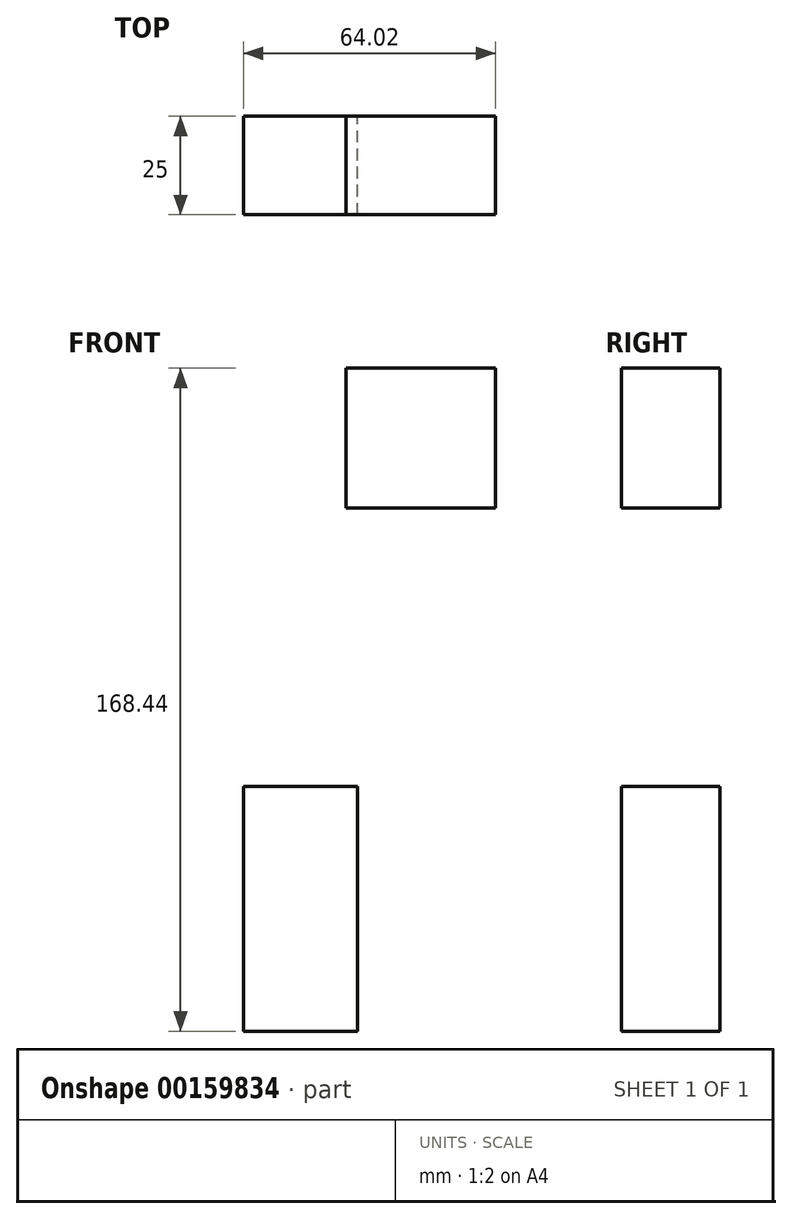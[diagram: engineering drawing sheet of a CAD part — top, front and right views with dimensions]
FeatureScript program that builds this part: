
annotation { "Feature Type Name" : "Feature", "Feature Type Description" : "" }
export const myFeature = defineFeature(function(context is Context, id is Id, definition is map)
    precondition{}
    {
        {
            var Q0;
            Q0=qCreatedBy(makeId("Front.planeOp"),FACE);
            var sketch = newSketch(context, id + "F0", { "sketchPlane" : qUnion([Q0])});
            skLineSegment(sketch, "E0.bottom", {"start": v(-161.5, 28.6) * mm, "end": v(-123.47, 28.6) * mm});
            skLineSegment(sketch, "E0.top", {"start": v(-161.5, -6.89) * mm, "end": v(-123.47, -6.89) * mm});
            skLineSegment(sketch, "E0.left", {"start": v(-161.5, 28.6) * mm, "end": v(-161.5, -6.89) * mm});
            skLineSegment(sketch, "E0.right", {"start": v(-123.47, 28.6) * mm, "end": v(-123.47, -6.89) * mm});
            skLineSegment(sketch, "E1.bottom", {"start": v(-187.49, -77.68) * mm, "end": v(-158.57, -77.68) * mm});
            skLineSegment(sketch, "E1.top", {"start": v(-187.49, -139.84) * mm, "end": v(-158.57, -139.84) * mm});
            skLineSegment(sketch, "E1.left", {"start": v(-187.49, -77.68) * mm, "end": v(-187.49, -139.84) * mm});
            skLineSegment(sketch, "E1.right", {"start": v(-158.57, -77.68) * mm, "end": v(-158.57, -139.84) * mm});
            skSolve(sketch);
        }
        {
            var Q0;
            Q0 = qSketchRegion(id + "F0", true);
            extrude(context, id + "F1", {"entities" : qUnion([Q0]), "depth" : 25 * mm});
        }
    });
